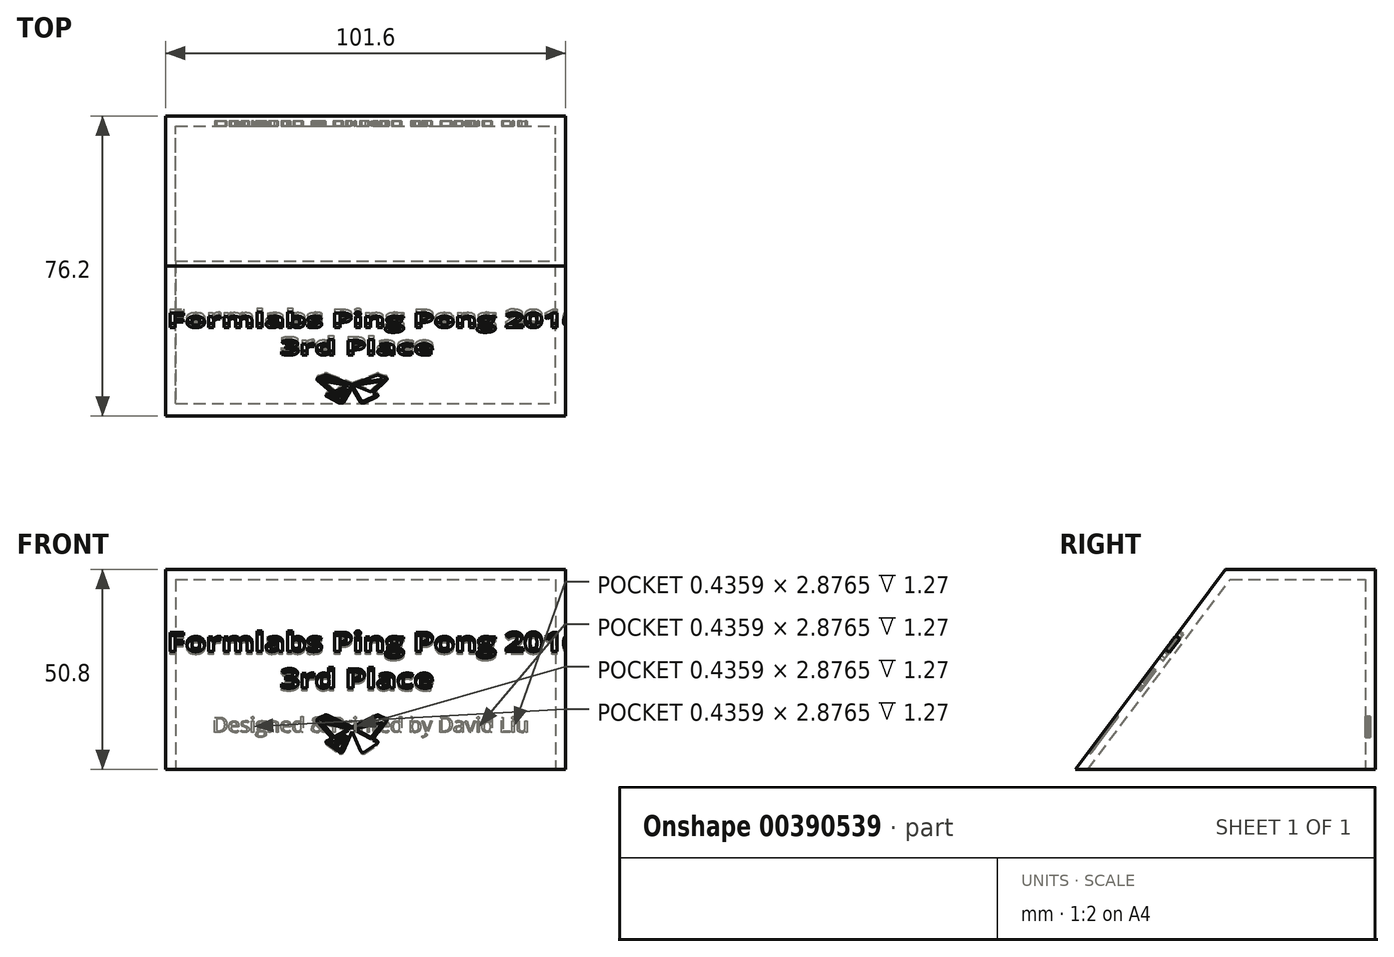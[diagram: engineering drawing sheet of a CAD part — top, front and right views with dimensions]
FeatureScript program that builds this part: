
annotation { "Feature Type Name" : "Feature", "Feature Type Description" : "" }
export const myFeature = defineFeature(function(context is Context, id is Id, definition is map)
    precondition{}
    {
        {
            var Q0;
            Q0=qCreatedBy(makeId("Top.planeOp"),FACE);
            var sketch = newSketch(context, id + "F0", { "sketchPlane" : qUnion([Q0])});
            skLineSegment(sketch, "E0.bottom", {"start": v(-33.87, 0) * mm, "end": v(67.73, 0) * mm});
            skLineSegment(sketch, "E0.top", {"start": v(-33.87, 76.2) * mm, "end": v(67.73, 76.2) * mm});
            skLineSegment(sketch, "E0.left", {"start": v(-33.87, 0) * mm, "end": v(-33.87, 76.2) * mm});
            skLineSegment(sketch, "E0.right", {"start": v(67.73, 0) * mm, "end": v(67.73, 76.2) * mm});
            skSolve(sketch);
        }
        {
            var Q0;
            Q0=makeQuery(id+"F0.imprint","IMPRINT",FACE,{"disambiguationData":[TD([[makeQuery(id+"F0.imprint","IMPRINT",EDGE,{"derivedFrom":sQuery(id+"F0.wireOp",EDGE,"E0.bottom")}),1.0]])]});
            extrude(context, id + "F1", {"entities" : qUnion([Q0]), "depth" : 50.8 * mm});
        }
        {
            var Q0;
            Q0=makeQuery(id+"F1.opExtrude","SWEPT_FACE",FACE,{"disambiguationData":[OSD([sQuery(id+"F0.wireOp",EDGE,"E0.right")])]});
            var sketch = newSketch(context, id + "F2", { "sketchPlane" : qUnion([Q0])});
            skLineSegment(sketch, "E1", {"start": v(0, 0) * mm, "end": v(38.1, 50.8) * mm});
            skLineSegment(sketch, "E2", {"start": v(38.1, 50.8) * mm, "end": v(0, 50.8) * mm});
            skLineSegment(sketch, "E3", {"start": v(0, 50.8) * mm, "end": v(0, 0) * mm});
            skSolve(sketch);
        }
        {
            var Q0;
            Q0=makeQuery(id+"F2.imprint","IMPRINT",FACE,{"disambiguationData":[TD([[makeQuery(id+"F2.imprint","IMPRINT",EDGE,{"derivedFrom":sQuery(id+"F2.wireOp",EDGE,"E1")}),1.0]])]});
            extrude(context, id + "F3", {"entities" : qUnion([Q0]), "operationType" : NewBodyOperationType.REMOVE, "endBound" : BoundingType.THROUGH_ALL, "oppositeDirection" : true, "depth" : 25.4 * mm});
        }
        {
            var Q0;
            Q0=makeQuery(id+"F1.opExtrude","CAP_FACE",FACE,{"disambiguationData":[OSD([sQuery(id+"F0.wireOp",EDGE,"E0.bottom"),sQuery(id+"F0.wireOp",EDGE,"E0.top"),sQuery(id+"F0.wireOp",EDGE,"E0.left"),sQuery(id+"F0.wireOp",EDGE,"E0.right")])],"isStart":true});
            shell(context, id + "F4", {"entities" : qUnion([Q0]), "thickness" : 2.54 * mm});
        }
        {
            var Q0;
            Q0=makeQuery(id+"F3.boolean.opBoolean","COPY",FACE,{"derivedFrom":makeQuery(id+"F3.opExtrude","SWEPT_FACE",FACE,{"disambiguationData":[OSD([sQuery(id+"F2.wireOp",EDGE,"E1")])]})});
            var sketch = newSketch(context, id + "F5", { "sketchPlane" : qUnion([Q0])});
            skText(sketch, "E4", { "text": "Formlabs Ping Pong 2016\n             3rd Place", "fontName": "OpenSans-Bold.ttf"});
            const initialGuessF5  = {"E4": [-0.03356, 0.03748, 1, 0, 0.00615]};
            skSetInitialGuess(sketch, initialGuessF5);
            skSolve(sketch);
        }
        {
            var Q0;
            Q0=qSketchRegion(id+"F5",true);
            extrude(context, id + "F6", {"entities" : qUnion([Q0]), "operationType" : NewBodyOperationType.REMOVE, "oppositeDirection" : true, "depth" : 1.27 * mm});
        }
        {
            var Q0;
            {var subQ1=sQuery(id+"F0.wireOp",EDGE,"E0.left");Q0=makeQuery(id+"F6.boolean.opBoolean","SPLIT",FACE,{"disambiguationData":[TD([makeQuery(id+"F1.opExtrude","SWEPT_FACE",FACE,{"disambiguationData":[OSD([subQ1])]})])],"derivedFrom":makeQuery(id+"F3.boolean.opBoolean","COPY",FACE,{"derivedFrom":makeQuery(id+"F3.opExtrude","SWEPT_FACE",FACE,{"disambiguationData":[OSD([sQuery(id+"F2.wireOp",EDGE,"E1")])]})})});}
            var sketch = newSketch(context, id + "F7", { "sketchPlane" : qUnion([Q0])});
            skLineSegment(sketch, "E5", {"start": v(7.36, 17.12) * mm, "end": v(13.48, 13.43) * mm});
            skLineSegment(sketch, "E6", {"start": v(13.48, 13.43) * mm, "end": v(19.63, 17.12) * mm});
            skLineSegment(sketch, "E7", {"start": v(21.3, 14.9) * mm, "end": v(14.26, 12.82) * mm});
            skLineSegment(sketch, "E8", {"start": v(14.26, 12.82) * mm, "end": v(18.27, 10.15) * mm});
            skLineSegment(sketch, "E9", {"start": v(18.27, 10.15) * mm, "end": v(21.3, 14.9) * mm});
            skLineSegment(sketch, "E10", {"start": v(22.26, 15.24) * mm, "end": v(18.81, 9.77) * mm});
            skLineSegment(sketch, "E11", {"start": v(18.81, 9.77) * mm, "end": v(19.74, 9.2) * mm});
            skLineSegment(sketch, "E12", {"start": v(12.62, 12.84) * mm, "end": v(8.98, 10.35) * mm});
            skLineSegment(sketch, "E13", {"start": v(8.98, 10.35) * mm, "end": v(5.87, 14.9) * mm});
            skLineSegment(sketch, "E14", {"start": v(5.87, 14.9) * mm, "end": v(12.62, 12.84) * mm});
            skLineSegment(sketch, "E15", {"start": v(11.48, 11.05) * mm, "end": v(9.95, 8.92) * mm});
            skLineSegment(sketch, "E16", {"start": v(9.95, 8.92) * mm, "end": v(9.46, 9.61) * mm});
            skLineSegment(sketch, "E17", {"start": v(9.46, 9.61) * mm, "end": v(11.48, 11.05) * mm});
            skLineSegment(sketch, "E18", {"start": v(12.25, 10.8) * mm, "end": v(10.73, 6.26) * mm});
            skLineSegment(sketch, "E19", {"start": v(10.73, 6.26) * mm, "end": v(7.92, 8.58) * mm});
            skLineSegment(sketch, "E20", {"start": v(7.92, 8.58) * mm, "end": v(8.75, 9.23) * mm});
            skLineSegment(sketch, "E21", {"start": v(7.06, 16.43) * mm, "end": v(10.55, 14.3) * mm});
            skLineSegment(sketch, "E22", {"start": v(10.55, 14.3) * mm, "end": v(5.8, 15.73) * mm});
            skLineSegment(sketch, "E23", {"start": v(5.8, 15.73) * mm, "end": v(7.06, 16.43) * mm});
            skLineSegment(sketch, "E24", {"start": v(13.5, 12.14) * mm, "end": v(15.58, 5.93) * mm});
            skLineSegment(sketch, "E25", {"start": v(13.5, 12.14) * mm, "end": v(11.34, 5.9) * mm});
            skLineSegment(sketch, "E26", {"start": v(7.14, 8.19) * mm, "end": v(10.22, 5.56) * mm});
            skLineSegment(sketch, "E27", {"start": v(8.25, 9.94) * mm, "end": v(7.08, 9.13) * mm});
            skLineSegment(sketch, "E28", {"start": v(5.04, 16.35) * mm, "end": v(6.52, 17.23) * mm});
            skLineSegment(sketch, "E29", {"start": v(20.34, 17.22) * mm, "end": v(22.03, 16.28) * mm});
            skLineSegment(sketch, "E30", {"start": v(16.53, 5.46) * mm, "end": v(19.73, 8.08) * mm});
            skLineSegment(sketch, "E31", {"start": v(12.25, 10.8) * mm, "end": v(10.27, 8.05) * mm});
            skArc(sketch, "E32", {"start": v(5.04, 16.35) * mm, "mid": v(4.6, 15.76) * mm, "end": v(4.7, 15.02) * mm});
            skArc(sketch, "E33", {"start": v(6.52, 17.23) * mm, "mid": v(6.96, 17.32) * mm, "end": v(7.36, 17.12) * mm});
            skArc(sketch, "E34", {"start": v(7.08, 9.13) * mm, "mid": v(6.85, 8.65) * mm, "end": v(7.14, 8.19) * mm});
            skArc(sketch, "E35", {"start": v(11.34, 5.9) * mm, "mid": v(10.87, 5.44) * mm, "end": v(10.22, 5.56) * mm});
            skArc(sketch, "E36", {"start": v(15.58, 5.93) * mm, "mid": v(15.96, 5.5) * mm, "end": v(16.53, 5.46) * mm});
            skArc(sketch, "E37", {"start": v(19.74, 9.2) * mm, "mid": v(20.04, 8.64) * mm, "end": v(19.73, 8.08) * mm});
            skArc(sketch, "E38", {"start": v(22.03, 16.28) * mm, "mid": v(22.38, 15.81) * mm, "end": v(22.26, 15.24) * mm});
            skArc(sketch, "E39", {"start": v(20.34, 17.22) * mm, "mid": v(19.97, 17.29) * mm, "end": v(19.63, 17.12) * mm});
            skArc(sketch, "E40", {"start": v(9.43, 8.25) * mm, "mid": v(9.8, 8) * mm, "end": v(10.27, 8.05) * mm});
            skLineSegment(sketch, "E41", {"start": v(4.7, 15.02) * mm, "end": v(8.25, 9.94) * mm});
            skLineSegment(sketch, "E42", {"start": v(8.75, 9.23) * mm, "end": v(9.43, 8.25) * mm});
            skSolve(sketch);
        }
        {
            var Q0;
            Q0=makeQuery(id+"F7.imprint","IMPRINT",FACE,{"disambiguationData":[TD([[makeQuery(id+"F7.imprint","IMPRINT",EDGE,{"derivedFrom":sQuery(id+"F7.wireOp",EDGE,"E5")}),-1.0]])]});
            extrude(context, id + "F8", {"entities" : qUnion([Q0]), "operationType" : NewBodyOperationType.REMOVE, "oppositeDirection" : true, "depth" : 0.64 * mm});
        }
        {
            var Q0;
            Q0=makeQuery(id+"F4.opShell","OFFSET_FACE",FACE,{"disambiguationData":[OSD([sQuery(id+"F0.wireOp",EDGE,"E0.top")])]});
            var sketch = newSketch(context, id + "F9", { "sketchPlane" : qUnion([Q0])});
            skText(sketch, "E43", { "text": "Designed & Printed by David Liu", "fontName": "OpenSans-Regular.ttf"});
            const initialGuessF9  = {"E43": [-0.02195, 0.00944, 1, 0, 0.00387]};
            skSetInitialGuess(sketch, initialGuessF9);
            skSolve(sketch);
        }
        {
            var Q0;
            Q0 = qSketchRegion(id + "F9", true);
            var Q1;
            Q1 = qConstructionFilter(qBodyType(qCreatedBy(id + "F9" ,EDGE), BodyType.WIRE), ConstructionObject.NO);
            extrude(context, id + "F10", {"entities" : qUnion([Q0]), "operationType" : NewBodyOperationType.REMOVE, "surfaceEntities" : qUnion([Q1]), "oppositeDirection" : true, "depth" : 1.27 * mm});
        }
    });
